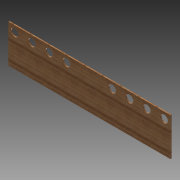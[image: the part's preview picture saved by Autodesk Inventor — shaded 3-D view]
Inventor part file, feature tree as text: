
AUTODESK INVENTOR PART (.ipt)
format: ipt  version: 2012 (Build 160160000, 160)  size: 102,400 bytes
history: native  units: in
note: dims shown in document units (in); Inventor stores cm internally (conversion verified against a paired STEP export)
features: extrude x1, sketch x1
ambient origin geometry x8: Origin, YZ Plane, XZ Plane, XY Plane, X Axis, Y Axis, Z Axis, Center Point
bodies: Solid1 (feature_tree)
feature tree (2):
  extrude  "Extrusion1"  Depth=32.0in
  sketch  "Sketch1"  dims[d0=7.5in d1=32.0in d11=0.25in d12=0.0in d13=1.5in d14=1.5in d15=9.0in d16=10.25in d17=3.4167in d18=3.4167in d19=1.25in d20=23.5in d21=1.25in d22=1.25in d23=1.25in d24=3.4167in d25=3.4167in]
